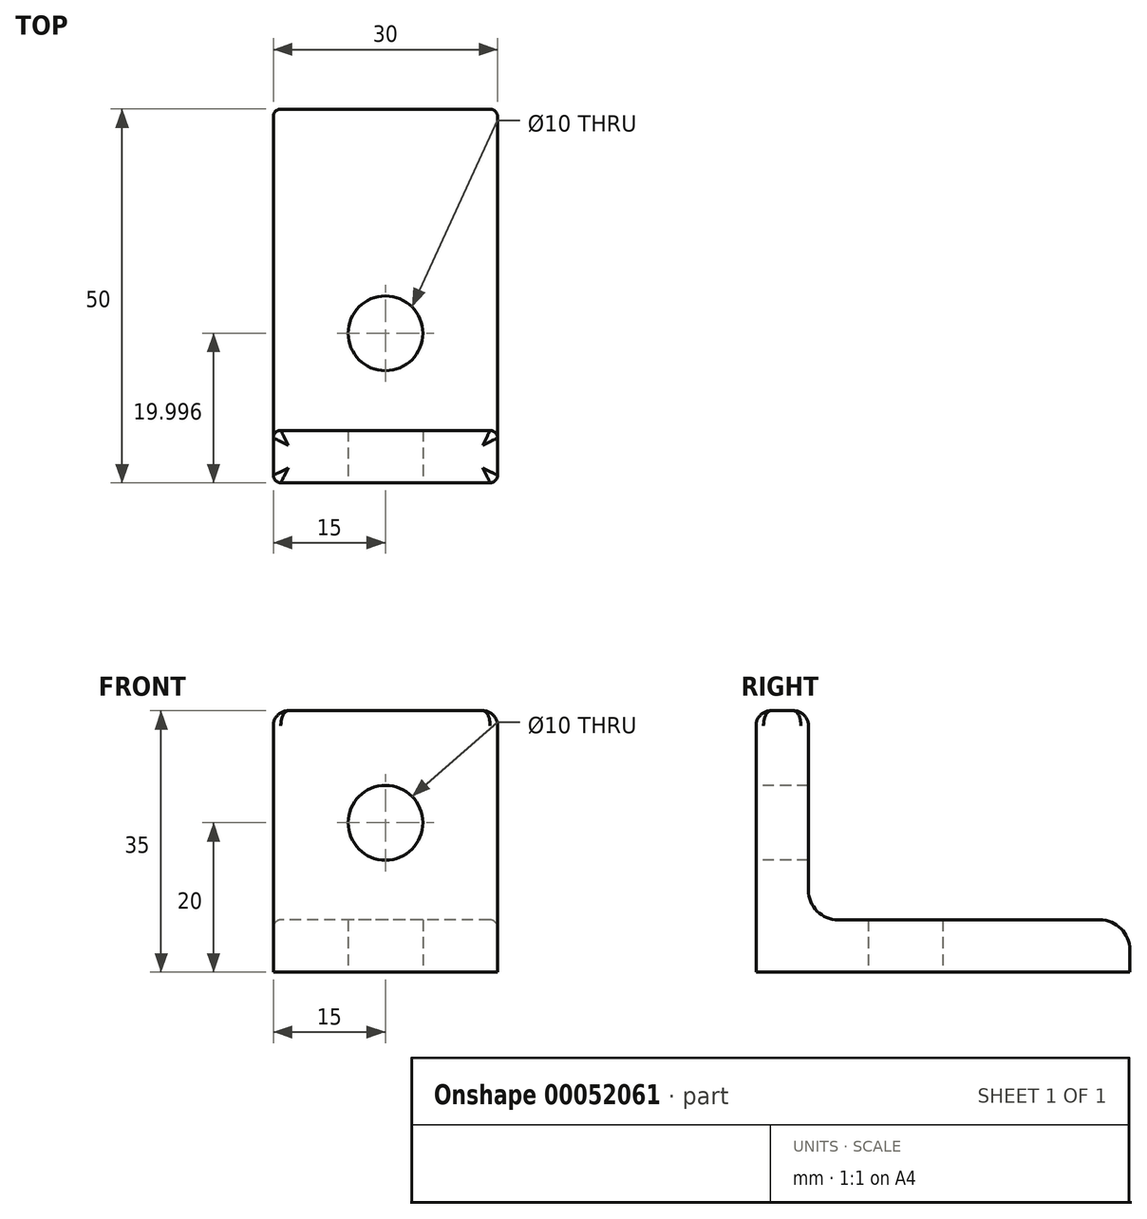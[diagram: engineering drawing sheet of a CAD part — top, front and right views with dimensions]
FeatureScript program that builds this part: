
annotation { "Feature Type Name" : "Feature", "Feature Type Description" : "" }
export const myFeature = defineFeature(function(context is Context, id is Id, definition is map)
    precondition{}
    {
        {
            var Q0;
            Q0=qCreatedBy(makeId("Right.planeOp"),FACE);
            var sketch = newSketch(context, id + "F0", { "sketchPlane" : qUnion([Q0])});
            skLineSegment(sketch, "E0", {"start": v(-9.55, 0) * mm, "end": v(-9.55, 35) * mm});
            skLineSegment(sketch, "E1", {"start": v(-9.55, 35) * mm, "end": v(-2.55, 35) * mm});
            skLineSegment(sketch, "E2", {"start": v(-2.55, 35) * mm, "end": v(-2.55, 7) * mm});
            skLineSegment(sketch, "E3", {"start": v(-2.55, 7) * mm, "end": v(40.45, 7) * mm});
            skLineSegment(sketch, "E4", {"start": v(40.45, 7) * mm, "end": v(40.45, 0) * mm});
            skLineSegment(sketch, "E5", {"start": v(40.45, 0) * mm, "end": v(-9.55, 0) * mm});
            skSolve(sketch);
        }
        {
            var Q0;
            Q0 = qSketchRegion(id + "F0", true);
            extrude(context, id + "F1", {"entities" : qUnion([Q0]), "depth" : 30 * mm});
        }
        {
            var Q0;
            Q0=makeQuery(id+"F1.opExtrude","SWEPT_EDGE",EDGE,{"disambiguationData":[OSD([sQuery(id+"F0.wireOp",EDGE,"E3"),sQuery(id+"F0.wireOp",EDGE,"E4")])]});
            var Q1;
            Q1=makeQuery(id+"F1.opExtrude","SWEPT_EDGE",EDGE,{"disambiguationData":[OSD([sQuery(id+"F0.wireOp",EDGE,"E2"),sQuery(id+"F0.wireOp",EDGE,"E3")])]});
            fillet(context, id + "F2", {"entities" : qUnion([Q0, Q1]), "radius" : 4 * mm, "tangentPropagation" : true, "allowEdgeOverflow" : false});
        }
        {
            var Q0;
            Q0=makeQuery(id+"F1.opExtrude","CAP_EDGE",EDGE,{"disambiguationData":[OSD([sQuery(id+"F0.wireOp",EDGE,"E3")])],"isStart":false});
            var Q1;
            Q1=makeQuery(id+"F1.opExtrude","CAP_EDGE",EDGE,{"disambiguationData":[OSD([sQuery(id+"F0.wireOp",EDGE,"E3")])],"isStart":true});
            var Q2;
            Q2=makeQuery(id+"F1.opExtrude","CAP_EDGE",EDGE,{"disambiguationData":[OSD([sQuery(id+"F0.wireOp",EDGE,"E2")])],"isStart":false});
            var Q3;
            Q3=makeQuery(id+"F1.opExtrude","CAP_EDGE",EDGE,{"disambiguationData":[OSD([sQuery(id+"F0.wireOp",EDGE,"E2")])],"isStart":true});
            var Q4;
            Q4=makeQuery(id+"F1.opExtrude","CAP_EDGE",EDGE,{"disambiguationData":[OSD([sQuery(id+"F0.wireOp",EDGE,"E0")])],"isStart":true});
            var Q5;
            Q5=makeQuery(id+"F1.opExtrude","CAP_EDGE",EDGE,{"disambiguationData":[OSD([sQuery(id+"F0.wireOp",EDGE,"E0")])],"isStart":false});
            fillet(context, id + "F3", {"entities" : qUnion([Q0, Q1, Q2, Q3, Q4, Q5]), "radius" : 1 * mm, "tangentPropagation" : true, "allowEdgeOverflow" : false});
        }
        {
            var Q0;
            Q0=makeQuery(id+"F1.opExtrude","SWEPT_FACE",FACE,{"disambiguationData":[OSD([sQuery(id+"F0.wireOp",EDGE,"E0")])]});
            var sketch = newSketch(context, id + "F4", { "sketchPlane" : qUnion([Q0])});
            skCircle(sketch, "E6", {"center": v(15, 20) * mm, "radius": 5 * mm});
            skSolve(sketch);
        }
        {
            var Q0;
            Q0 = qSketchRegion(id + "F4", true);
            extrude(context, id + "F5", {"entities" : qUnion([Q0]), "operationType" : NewBodyOperationType.REMOVE, "oppositeDirection" : true, "depth" : 8 * mm});
        }
        {
            var Q0;
            Q0=makeQuery(id+"F1.opExtrude","SWEPT_FACE",FACE,{"disambiguationData":[OSD([sQuery(id+"F0.wireOp",EDGE,"E5")])]});
            var sketch = newSketch(context, id + "F6", { "sketchPlane" : qUnion([Q0])});
            skCircle(sketch, "E7", {"center": v(15, -10.45) * mm, "radius": 5 * mm});
            skSolve(sketch);
        }
        {
            var Q0;
            Q0 = qSketchRegion(id + "F6", true);
            extrude(context, id + "F7", {"entities" : qUnion([Q0]), "operationType" : NewBodyOperationType.REMOVE, "oppositeDirection" : true, "depth" : 8 * mm});
        }
        {
            var Q0;
            Q0=makeQuery(id+"F1.opExtrude","SWEPT_EDGE",EDGE,{"disambiguationData":[OSD([sQuery(id+"F0.wireOp",EDGE,"E1"),sQuery(id+"F0.wireOp",EDGE,"E2")])]});
            fillet(context, id + "F8", {"entities" : qUnion([Q0]), "radius" : 2 * mm, "tangentPropagation" : true, "allowEdgeOverflow" : false});
        }
    });
